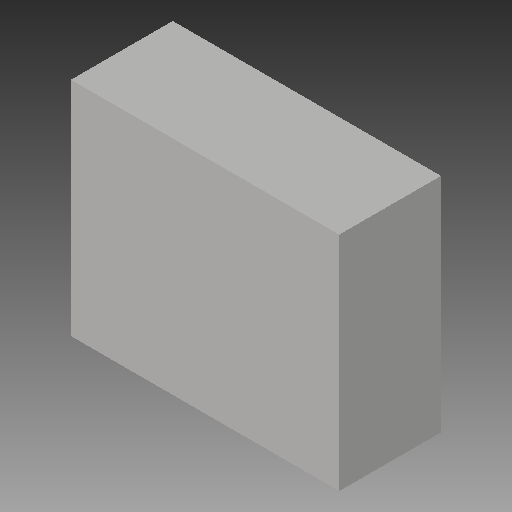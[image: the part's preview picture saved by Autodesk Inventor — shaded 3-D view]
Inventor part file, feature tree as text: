
AUTODESK INVENTOR PART (.ipt)
format: ipt  version: 2018 (Build 220112000, 112)  size: 82,944 bytes
history: native  units: mm
features: extrude x1, sketch x1
ambient origin geometry x8: Origin, YZ Plane, XZ Plane, XY Plane, X Axis, Y Axis, Z Axis, Center Point
bodies: Solid1 (feature_tree)
feature tree (2):
  extrude  "Extrusion1"  Depth=48.0mm
  sketch  "Sketch1"  dims[d0=58.0mm d1=48.0mm d2=22.0mm d3=0.0mm]
